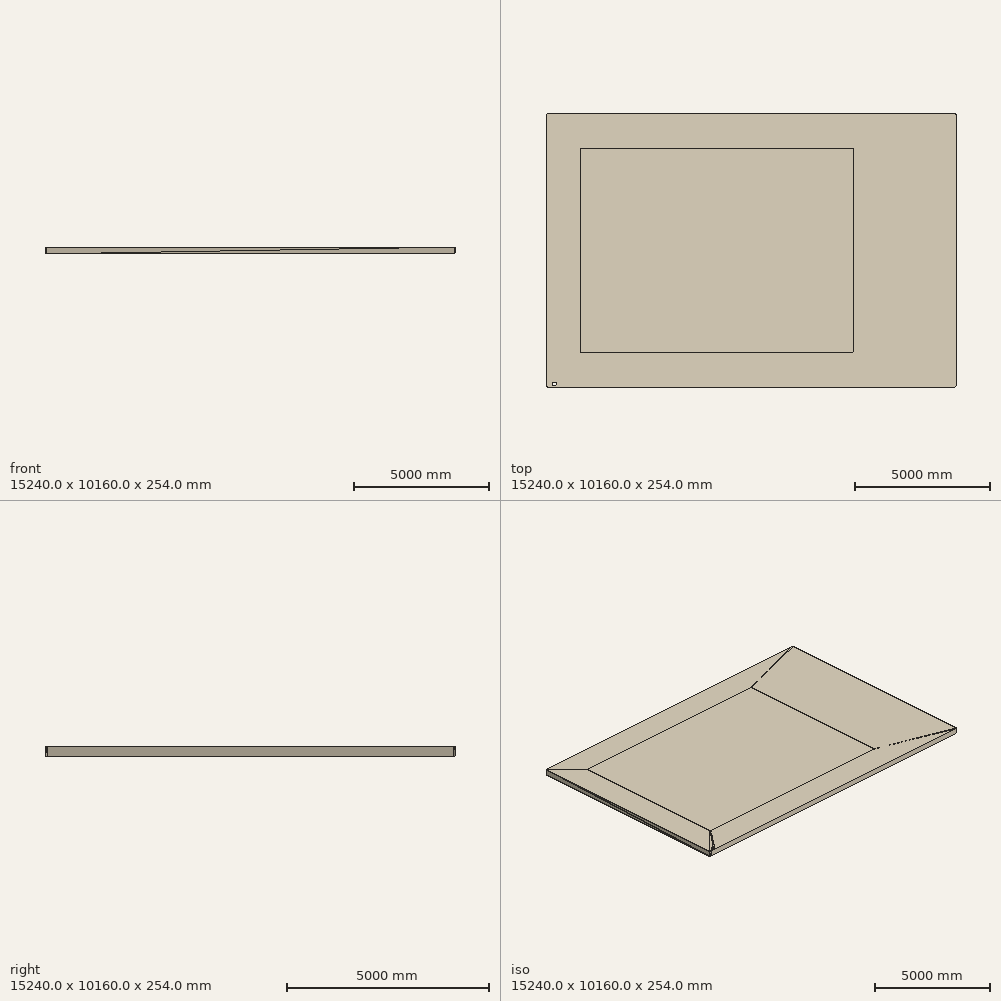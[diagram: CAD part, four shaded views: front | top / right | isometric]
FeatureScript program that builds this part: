
annotation { "Feature Type Name" : "Feature", "Feature Type Description" : "" }
export const myFeature = defineFeature(function(context is Context, id is Id, definition is map)
    precondition{}
    {
        {
            var Q0;
            Q0=qCreatedBy(makeId("Top.planeOp"),FACE);
            var sketch = newSketch(context, id + "F0", { "sketchPlane" : qUnion([Q0])});
            skLineSegment(sketch, "E0.bottom", {"start": v(-60.59, 9951.54) * mm, "end": v(15077.81, 9951.54) * mm});
            skLineSegment(sketch, "E0.top", {"start": v(-60.59, -208.46) * mm, "end": v(15077.81, -208.46) * mm});
            skLineSegment(sketch, "E0.left", {"start": v(-111.39, 9900.74) * mm, "end": v(-111.39, -157.66) * mm});
            skLineSegment(sketch, "E0.right", {"start": v(15128.61, 9900.74) * mm, "end": v(15128.61, -157.66) * mm});
            skLineSegment(sketch, "E1.bottom", {"start": v(121.62, -21.83) * mm, "end": v(245.71, -21.83) * mm});
            skLineSegment(sketch, "E1.top", {"start": v(121.62, -134.02) * mm, "end": v(245.71, -134.02) * mm});
            skLineSegment(sketch, "E1.left", {"start": v(121.62, -21.83) * mm, "end": v(121.62, -134.02) * mm});
            skLineSegment(sketch, "E1.right", {"start": v(245.71, -21.83) * mm, "end": v(245.71, -134.02) * mm});
            skPoint(sketch, "E2.visualSharp", {"position": v(-111.39, 9951.54) * mm});
            skArc(sketch, "E2.filletArc", {"start": v(-60.59, 9951.54) * mm, "mid": v(-96.5, 9936.66) * mm, "end": v(-111.39, 9900.74) * mm});
            skPoint(sketch, "E3.visualSharp", {"position": v(15128.61, 9951.54) * mm});
            skArc(sketch, "E3.filletArc", {"start": v(15128.61, 9900.74) * mm, "mid": v(15113.73, 9936.66) * mm, "end": v(15077.81, 9951.54) * mm});
            skPoint(sketch, "E4.visualSharp", {"position": v(15128.61, -208.46) * mm});
            skArc(sketch, "E4.filletArc", {"start": v(15077.81, -208.46) * mm, "mid": v(15113.73, -193.58) * mm, "end": v(15128.61, -157.66) * mm});
            skPoint(sketch, "E5.visualSharp", {"position": v(-111.39, -208.46) * mm});
            skArc(sketch, "E5.filletArc", {"start": v(-111.39, -157.66) * mm, "mid": v(-96.5, -193.58) * mm, "end": v(-60.59, -208.46) * mm});
            skSolve(sketch);
        }
        {
            var Q0;
            Q0=makeQuery(id+"F0.imprint","IMPRINT",FACE,{"disambiguationData":[TD([[makeQuery(id+"F0.imprint","IMPRINT",EDGE,{"derivedFrom":sQuery(id+"F0.wireOp",EDGE,"E0.bottom")}),-1.0]])]});
            extrude(context, id + "F1", {"entities" : qUnion([Q0]), "depth" : 254 * mm, "offsetDistance" : 25.4 * mm});
        }
        {
            var Q0;
            Q0=makeQuery(id+"F1.opExtrude","CAP_FACE",FACE,{"disambiguationData":[OSD([sQuery(id+"F0.wireOp",EDGE,"E0.bottom"),sQuery(id+"F0.wireOp",EDGE,"E0.top"),sQuery(id+"F0.wireOp",EDGE,"E0.left"),sQuery(id+"F0.wireOp",EDGE,"E0.right"),sQuery(id+"F0.wireOp",EDGE,"E1.bottom"),sQuery(id+"F0.wireOp",EDGE,"E1.top"),sQuery(id+"F0.wireOp",EDGE,"E1.left"),sQuery(id+"F0.wireOp",EDGE,"E1.right"),sQuery(id+"F0.wireOp",EDGE,"E2.filletArc"),sQuery(id+"F0.wireOp",EDGE,"E3.filletArc"),sQuery(id+"F0.wireOp",EDGE,"E4.filletArc"),sQuery(id+"F0.wireOp",EDGE,"E5.filletArc")])],"isStart":false});
            var sketch = newSketch(context, id + "F2", { "sketchPlane" : qUnion([Q0])});
            skLineSegment(sketch, "E6.bottom", {"start": v(11293.21, 1061.54) * mm, "end": v(1184.01, 1061.54) * mm});
            skLineSegment(sketch, "E6.top", {"start": v(11293.21, 8681.54) * mm, "end": v(1184.01, 8681.54) * mm});
            skLineSegment(sketch, "E6.left", {"start": v(11318.61, 1086.94) * mm, "end": v(11318.61, 8656.14) * mm});
            skLineSegment(sketch, "E6.right", {"start": v(1158.61, 1086.94) * mm, "end": v(1158.61, 8656.14) * mm});
            skPoint(sketch, "E7.visualSharp", {"position": v(11318.61, 1061.54) * mm});
            skArc(sketch, "E7.filletArc", {"start": v(11293.21, 1061.54) * mm, "mid": v(11311.17, 1068.98) * mm, "end": v(11318.61, 1086.94) * mm});
            skPoint(sketch, "E8.visualSharp", {"position": v(11318.61, 8681.54) * mm});
            skArc(sketch, "E8.filletArc", {"start": v(11318.61, 8656.14) * mm, "mid": v(11311.17, 8674.1) * mm, "end": v(11293.21, 8681.54) * mm});
            skPoint(sketch, "E9.visualSharp", {"position": v(1158.61, 8681.54) * mm});
            skArc(sketch, "E9.filletArc", {"start": v(1184.01, 8681.54) * mm, "mid": v(1166.05, 8674.1) * mm, "end": v(1158.61, 8656.14) * mm});
            skPoint(sketch, "E10.visualSharp", {"position": v(1158.61, 1061.54) * mm});
            skArc(sketch, "E10.filletArc", {"start": v(1158.61, 1086.94) * mm, "mid": v(1166.05, 1068.98) * mm, "end": v(1184.01, 1061.54) * mm});
            skLineSegment(sketch, "E11.0", {"start": v(11293.21, 1067.9) * mm, "end": v(1184.01, 1067.9) * mm});
            skArc(sketch, "E11.1", {"start": v(1164.96, 1086.94) * mm, "mid": v(1170.54, 1073.47) * mm, "end": v(1184.01, 1067.9) * mm});
            skArc(sketch, "E11.2", {"start": v(11293.21, 1067.9) * mm, "mid": v(11306.68, 1073.47) * mm, "end": v(11312.26, 1086.94) * mm});
            skLineSegment(sketch, "E11.3", {"start": v(1164.96, 1086.94) * mm, "end": v(1164.96, 8656.14) * mm});
            skLineSegment(sketch, "E11.4", {"start": v(11312.26, 1086.94) * mm, "end": v(11312.26, 8656.14) * mm});
            skArc(sketch, "E11.5", {"start": v(11312.26, 8656.14) * mm, "mid": v(11306.68, 8669.61) * mm, "end": v(11293.21, 8675.2) * mm});
            skLineSegment(sketch, "E11.6", {"start": v(11293.21, 8675.2) * mm, "end": v(1184.01, 8675.2) * mm});
            skArc(sketch, "E11.7", {"start": v(1184.01, 8675.2) * mm, "mid": v(1170.54, 8669.61) * mm, "end": v(1164.96, 8656.14) * mm});
            skSolve(sketch);
        }
        {
            var Q0;
            Q0 = qSketchRegion(id + "F2", true);
            extrude(context, id + "F3", {"entities" : qUnion([Q0]), "operationType" : NewBodyOperationType.REMOVE, "oppositeDirection" : true, "depth" : 12.7 * mm, "offsetDistance" : 25.4 * mm});
        }
    });
